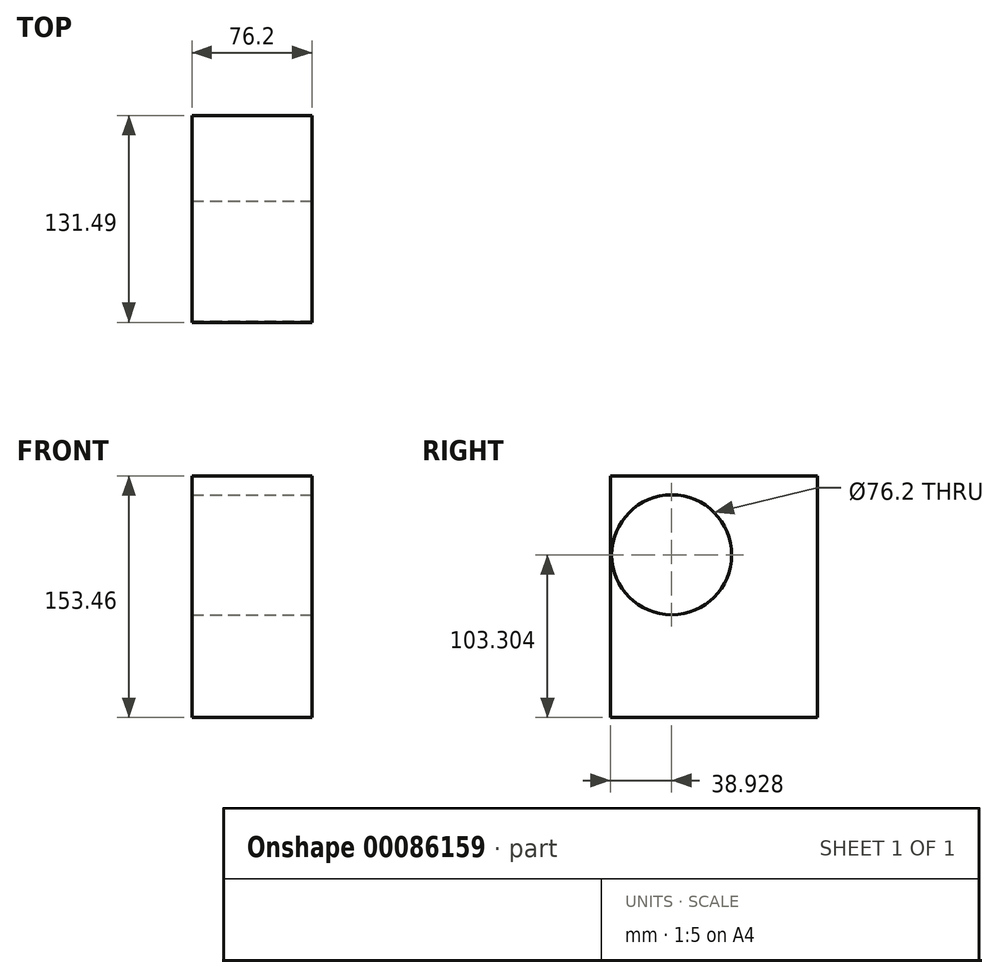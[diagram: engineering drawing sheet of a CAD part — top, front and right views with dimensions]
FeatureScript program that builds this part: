
annotation { "Feature Type Name" : "Feature", "Feature Type Description" : "" }
export const myFeature = defineFeature(function(context is Context, id is Id, definition is map)
    precondition{}
    {
        {
            var Q0;
            Q0=qCreatedBy(makeId("Right.planeOp"),FACE);
            var sketch = newSketch(context, id + "F0", { "sketchPlane" : qUnion([Q0])});
            skLineSegment(sketch, "E0.bottom", {"start": v(0, 0) * mm, "end": v(131.5, 0) * mm});
            skLineSegment(sketch, "E0.top", {"start": v(0, -153.46) * mm, "end": v(131.5, -153.46) * mm});
            skLineSegment(sketch, "E0.left", {"start": v(0, 0) * mm, "end": v(0, -153.46) * mm});
            skLineSegment(sketch, "E0.right", {"start": v(131.5, 0) * mm, "end": v(131.5, -153.46) * mm});
            skSolve(sketch);
        }
        {
            var Q0;
            Q0 = qSketchRegion(id + "F0", true);
            extrude(context, id + "F1", {"entities" : qUnion([Q0]), "depth" : 76.2 * mm});
        }
        {
            var Q0;
            Q0=makeQuery(id+"F1.opExtrude","CAP_FACE",FACE,{"disambiguationData":[OSD([sQuery(id+"F0.wireOp",EDGE,"E0.bottom"),sQuery(id+"F0.wireOp",EDGE,"E0.top"),sQuery(id+"F0.wireOp",EDGE,"E0.left"),sQuery(id+"F0.wireOp",EDGE,"E0.right")])],"isStart":false});
            var sketch = newSketch(context, id + "F2", { "sketchPlane" : qUnion([Q0])});
            skCircle(sketch, "E1", {"center": v(38.93, -50.16) * mm, "radius": 18.98 * mm});
            skSolve(sketch);
        }
        {
            var Q0;
            Q0=sQuery(id+"F2.wireOp",VERTEX,"E1.center");
            var Q1;
            Q1=makeQuery(id+"F1.opExtrude","SWEPT_BODY",BODY,{"disambiguationData":[OSD([sQuery(id+"F0.wireOp",EDGE,"E0.bottom"),sQuery(id+"F0.wireOp",EDGE,"E0.top"),sQuery(id+"F0.wireOp",EDGE,"E0.left"),sQuery(id+"F0.wireOp",EDGE,"E0.right")])]});
            hole(context, id + "F3", {"style" : HoleStyle.SIMPLE, "endStyle" : HoleEndStyle.THROUGH, "holeDiameter" : 76.2 * mm, "locations" : qUnion([Q0]), "scope" : qUnion([Q1]), "isTappedThrough" : true});
        }
    });
